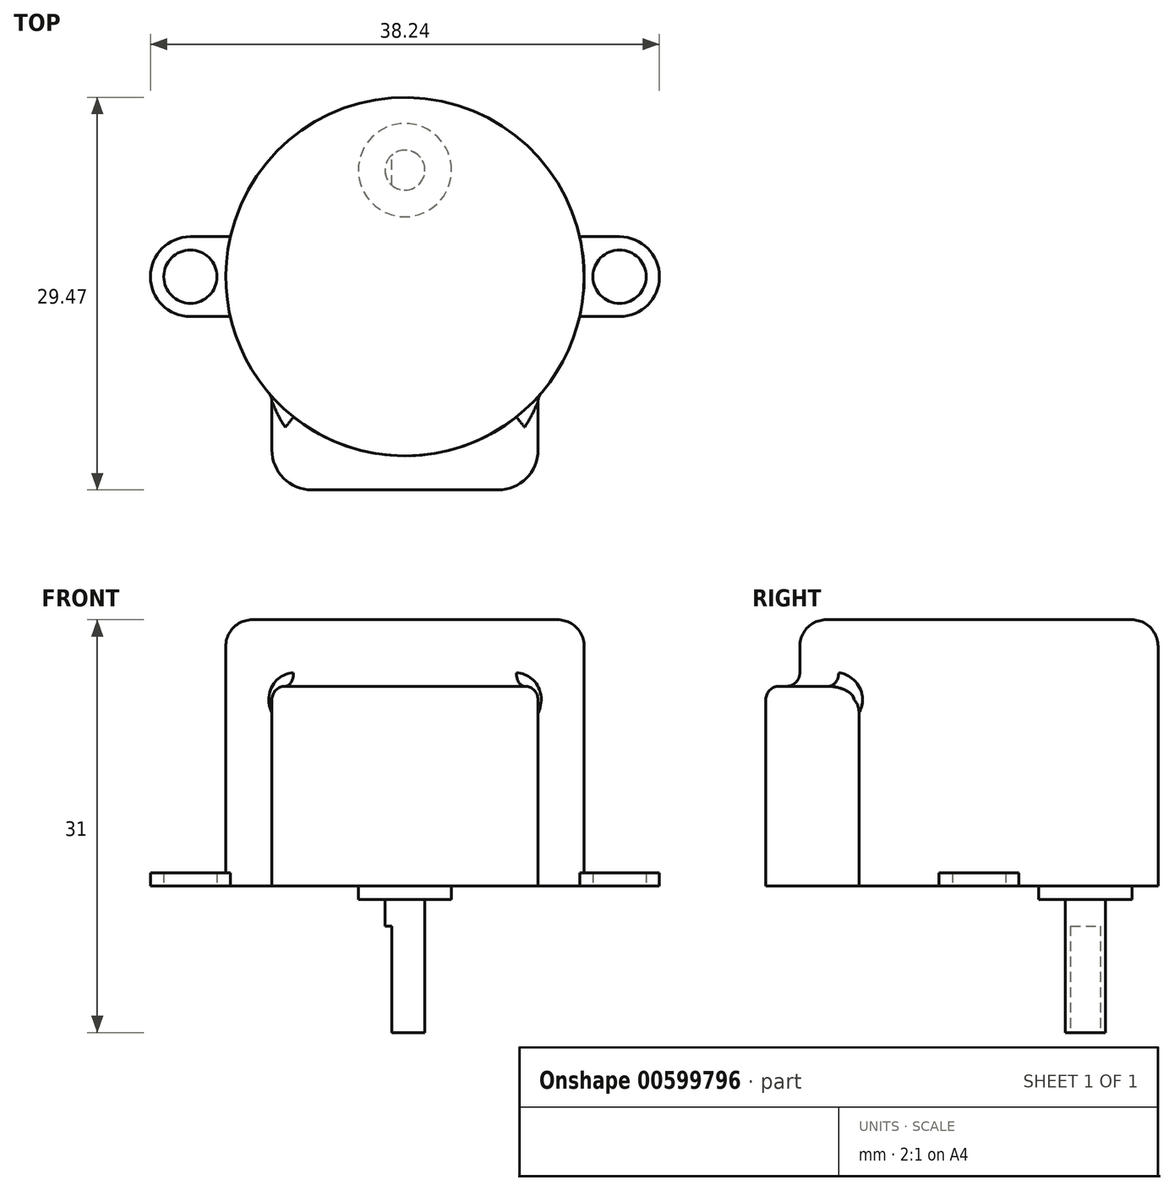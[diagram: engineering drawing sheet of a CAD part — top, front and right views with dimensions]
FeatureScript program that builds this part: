
annotation { "Feature Type Name" : "Feature", "Feature Type Description" : "" }
export const myFeature = defineFeature(function(context is Context, id is Id, definition is map)
    precondition{}
    {
        {
            var Q0;
            Q0=qCreatedBy(makeId("Top.planeOp"),FACE);
            var sketch = newSketch(context, id + "F0", { "sketchPlane" : qUnion([Q0])});
            skCircle(sketch, "E0", {"center": v(0, 0) * mm, "radius": 13.46 * mm});
            skSolve(sketch);
        }
        {
            var Q0;
            Q0=makeQuery(id+"F0.imprint","IMPRINT",FACE,{"disambiguationData":[TD([[makeQuery(id+"F0.imprint","IMPRINT",EDGE,{"derivedFrom":sQuery(id+"F0.wireOp",EDGE,"E0")}),1.0]])]});
            extrude(context, id + "F1", {"entities" : qUnion([Q0]), "depth" : 20 * mm, "offsetDistance" : 25 * mm});
        }
        {
            var Q0;
            Q0=makeQuery(id+"F1.opExtrude","CAP_EDGE",EDGE,{"disambiguationData":[OSD([sQuery(id+"F0.wireOp",EDGE,"E0")])],"isStart":false});
            fillet(context, id + "F2", {"entities" : qUnion([Q0]), "radius" : 2 * mm, "tangentPropagation" : true, "allowEdgeOverflow" : false});
        }
        {
            var Q0;
            Q0=qCreatedBy(makeId("Top.planeOp"),FACE);
            var sketch = newSketch(context, id + "F3", { "sketchPlane" : qUnion([Q0])});
            skLineSegment(sketch, "E1.bottom", {"start": v(10, -9.01) * mm, "end": v(-10, -9.01) * mm});
            skLineSegment(sketch, "E1.top", {"start": v(10, -16.01) * mm, "end": v(-10, -16.01) * mm});
            skLineSegment(sketch, "E1.left", {"start": v(10, -9.01) * mm, "end": v(10, -16.01) * mm});
            skLineSegment(sketch, "E1.right", {"start": v(-10, -9.01) * mm, "end": v(-10, -16.01) * mm});
            skSolve(sketch);
        }
        {
            var Q0;
            Q0=makeQuery(id+"F3.imprint","IMPRINT",FACE,{"disambiguationData":[TD([[makeQuery(id+"F3.imprint","IMPRINT",EDGE,{"derivedFrom":sQuery(id+"F3.wireOp",EDGE,"E1.bottom")}),1.0]])]});
            extrude(context, id + "F4", {"entities" : qUnion([Q0]), "operationType" : NewBodyOperationType.ADD, "depth" : 15 * mm, "offsetDistance" : 25 * mm});
        }
        {
            var Q0;
            Q0=makeQuery(id+"F4.opExtrude","SWEPT_EDGE",EDGE,{"disambiguationData":[OSD([sQuery(id+"F3.wireOp",EDGE,"E1.top"),sQuery(id+"F3.wireOp",EDGE,"E1.right")])]});
            var Q1;
            Q1=makeQuery(id+"F4.opExtrude","SWEPT_EDGE",EDGE,{"disambiguationData":[OSD([sQuery(id+"F3.wireOp",EDGE,"E1.top"),sQuery(id+"F3.wireOp",EDGE,"E1.left")])]});
            fillet(context, id + "F5", {"entities" : qUnion([Q0, Q1]), "radius" : 3 * mm, "tangentPropagation" : true, "allowEdgeOverflow" : false});
        }
        {
            var Q0;
            Q0=makeQuery(id+"F4.opExtrude","CAP_FACE",FACE,{"disambiguationData":[OSD([sQuery(id+"F3.wireOp",EDGE,"E1.bottom"),sQuery(id+"F3.wireOp",EDGE,"E1.top"),sQuery(id+"F3.wireOp",EDGE,"E1.left"),sQuery(id+"F3.wireOp",EDGE,"E1.right")])],"isStart":false});
            fillet(context, id + "F6", {"entities" : qUnion([Q0]), "radius" : 1 * mm, "tangentPropagation" : true, "allowEdgeOverflow" : false});
        }
        {
            var Q0;
            Q0=makeQuery(id+"F4.boolean.opBoolean","MERGE",FACE,{"derivedFrom":[makeQuery(id+"F1.opExtrude","CAP_FACE",FACE,{"disambiguationData":[OSD([sQuery(id+"F0.wireOp",EDGE,"E0")])],"isStart":true}),makeQuery(id+"F4.opExtrude","CAP_FACE",FACE,{"disambiguationData":[OSD([sQuery(id+"F3.wireOp",EDGE,"E1.bottom"),sQuery(id+"F3.wireOp",EDGE,"E1.top"),sQuery(id+"F3.wireOp",EDGE,"E1.left"),sQuery(id+"F3.wireOp",EDGE,"E1.right")])],"isStart":true})]});
            var sketch = newSketch(context, id + "F7", { "sketchPlane" : qUnion([Q0])});
            skCircle(sketch, "E2", {"center": v(0, -8) * mm, "radius": 3.5 * mm});
            skSolve(sketch);
        }
        {
            var Q0;
            Q0=makeQuery(id+"F7.imprint","IMPRINT",FACE,{"disambiguationData":[TD([[makeQuery(id+"F7.imprint","IMPRINT",EDGE,{"derivedFrom":sQuery(id+"F7.wireOp",EDGE,"E2")}),1.0]])]});
            var Q1;
            Q1=makeQuery(id+"F7.imprint","IMPRINT",FACE,{"disambiguationData":[TD([[makeQuery(id+"F7.imprint","IMPRINT",EDGE,{"derivedFrom":sQuery(id+"F7.wireOp",EDGE,"TeglMqy4-CWTu-kgJV-pBj6-zsEYN7U3uUOE")}),1.0]])]});
            var Q2;
            Q2=sQuery(id+"F7.wireOp",EDGE,"E2");
            extrude(context, id + "F8", {"entities" : qUnion([Q0, Q1]), "operationType" : NewBodyOperationType.ADD, "surfaceEntities" : qUnion([Q2]), "depth" : 1 * mm, "offsetDistance" : 25 * mm});
        }
        {
            var Q0;
            Q0=makeQuery(id+"F8.opExtrude","CAP_FACE",FACE,{"disambiguationData":[OSD([sQuery(id+"F7.wireOp",EDGE,"E2")])],"isStart":false});
            var sketch = newSketch(context, id + "F9", { "sketchPlane" : qUnion([Q0])});
            skCircle(sketch, "E3", {"center": v(0, -8) * mm, "radius": 1.5 * mm});
            skSolve(sketch);
        }
        {
            var Q0;
            Q0=makeQuery(id+"F9.imprint","IMPRINT",FACE,{"disambiguationData":[TD([[makeQuery(id+"F9.imprint","IMPRINT",EDGE,{"derivedFrom":sQuery(id+"F9.wireOp",EDGE,"E3")}),1.0]])]});
            extrude(context, id + "F10", {"entities" : qUnion([Q0]), "depth" : 10 * mm, "offsetDistance" : 25 * mm});
        }
        {
            var Q0;
            Q0=makeQuery(id+"F10.opExtrude","CAP_FACE",FACE,{"disambiguationData":[OSD([sQuery(id+"F9.wireOp",EDGE,"E3")])],"isStart":false});
            var sketch = newSketch(context, id + "F11", { "sketchPlane" : qUnion([Q0])});
            skLineSegment(sketch, "E4", {"start": v(-1, -6.88) * mm, "end": v(-1, -9.12) * mm});
            skArc(sketch, "E5", {"start": v(-1, -6.88) * mm, "mid": v(-1.5, -8) * mm, "end": v(-1, -9.12) * mm});
            skSolve(sketch);
        }
        {
            var Q0;
            Q0=makeQuery(id+"F11.imprint","IMPRINT",FACE,{"disambiguationData":[TD([[makeQuery(id+"F11.imprint","IMPRINT",EDGE,{"derivedFrom":sQuery(id+"F11.wireOp",EDGE,"E4")}),-1.0]])]});
            extrude(context, id + "F12", {"entities" : qUnion([Q0]), "operationType" : NewBodyOperationType.REMOVE, "oppositeDirection" : true, "depth" : 8 * mm, "offsetDistance" : 25 * mm});
        }
        {
            var Q0;
            Q0=makeQuery(id+"F4.boolean.opBoolean","MERGE",FACE,{"derivedFrom":[makeQuery(id+"F1.opExtrude","CAP_FACE",FACE,{"disambiguationData":[OSD([sQuery(id+"F0.wireOp",EDGE,"E0")])],"isStart":true}),makeQuery(id+"F4.opExtrude","CAP_FACE",FACE,{"disambiguationData":[OSD([sQuery(id+"F3.wireOp",EDGE,"E1.bottom"),sQuery(id+"F3.wireOp",EDGE,"E1.top"),sQuery(id+"F3.wireOp",EDGE,"E1.left"),sQuery(id+"F3.wireOp",EDGE,"E1.right")])],"isStart":true})]});
            var sketch = newSketch(context, id + "F13", { "sketchPlane" : qUnion([Q0])});
            skLineSegment(sketch, "E6", {"start": v(-13.12, -3) * mm, "end": v(-16.12, -3) * mm});
            skLineSegment(sketch, "E7", {"start": v(-16.12, 3) * mm, "end": v(-13.12, 3) * mm});
            skArc(sketch, "E8", {"start": v(-16.12, -3) * mm, "mid": v(-19.12, 0) * mm, "end": v(-16.12, 3) * mm});
            skCircle(sketch, "E9", {"center": v(-16.12, 0) * mm, "radius": 2 * mm});
            skArc(sketch, "E10.MirrorCS", {"start": v(16.12, -3) * mm, "mid": v(19.12, 0) * mm, "end": v(16.12, 3) * mm});
            skCircle(sketch, "E11.MirrorC", {"center": v(16.12, 0) * mm, "radius": 2 * mm});
            skLineSegment(sketch, "E12.MirrorCS", {"start": v(16.12, 3) * mm, "end": v(13.12, 3) * mm});
            skLineSegment(sketch, "E13.MirrorCS", {"start": v(13.12, -3) * mm, "end": v(16.12, -3) * mm});
            skSolve(sketch);
        }
        {
            var Q0;
            {var subQ0=sQuery(id+"F13.wireOp",EDGE,"E6");Q0=makeQuery(id+"F13.imprint","IMPRINT",FACE,{"disambiguationData":[TD([[makeQuery(id+"F13.imprint","IMPRINT",EDGE,{"derivedFrom":subQ0}),-1.0]])]});}
            var Q1;
            Q1=makeQuery(id+"F13.imprint","IMPRINT",FACE,{"disambiguationData":[TD([[makeQuery(id+"F13.imprint","IMPRINT",EDGE,{"derivedFrom":sQuery(id+"F13.wireOp",EDGE,"E10.MirrorCS")}),1.0]])]});
            extrude(context, id + "F14", {"entities" : qUnion([Q0, Q1]), "operationType" : NewBodyOperationType.ADD, "oppositeDirection" : true, "depth" : 1 * mm, "offsetDistance" : 25 * mm});
        }
    });
